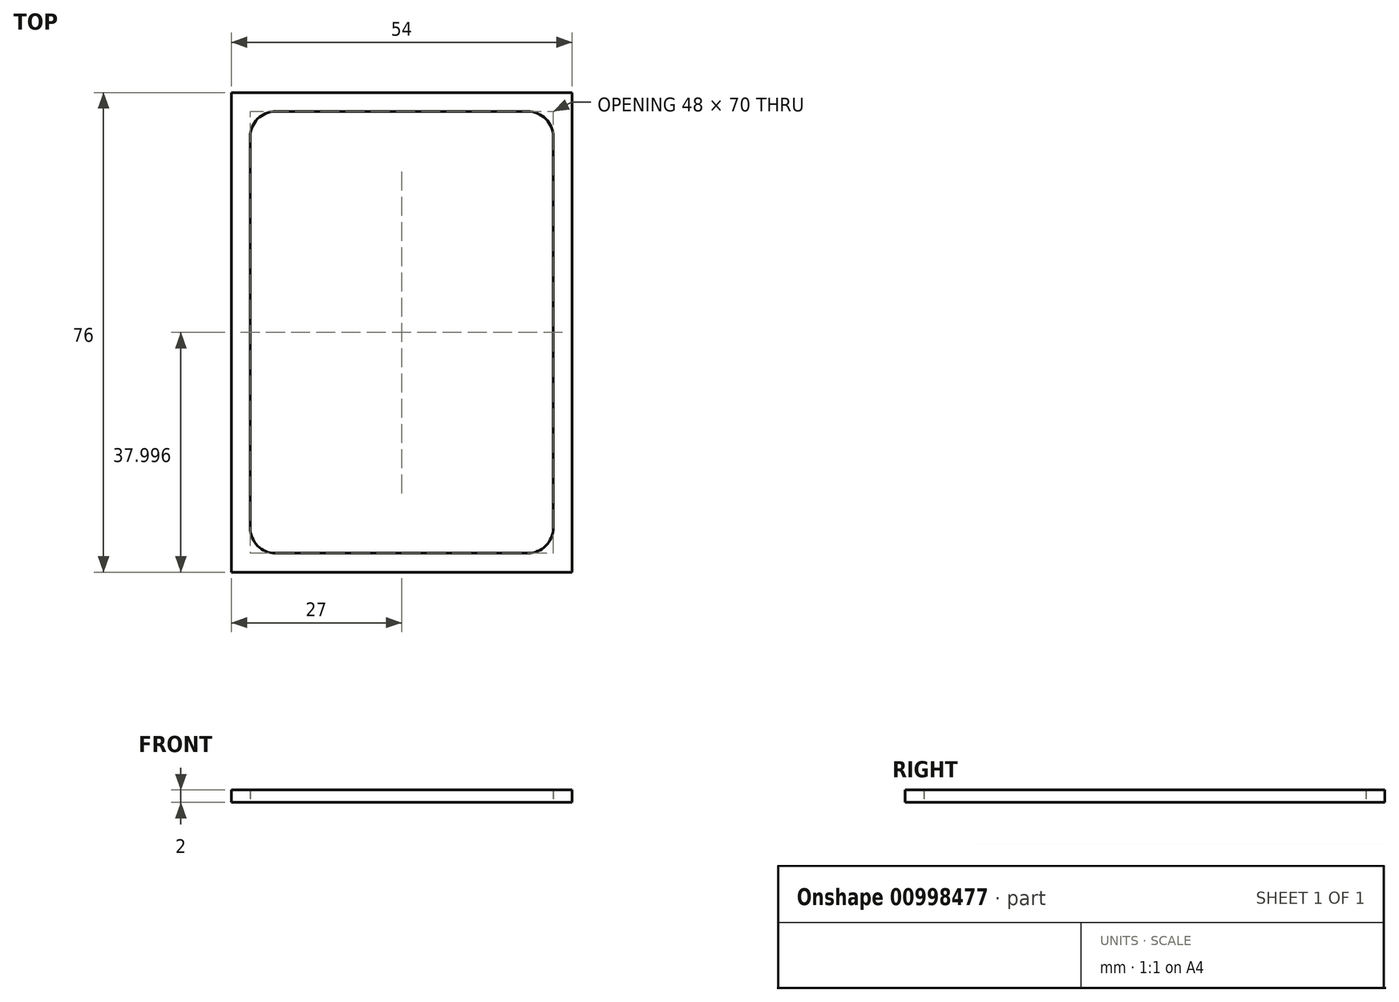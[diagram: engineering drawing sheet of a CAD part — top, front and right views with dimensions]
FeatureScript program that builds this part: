
annotation { "Feature Type Name" : "Feature", "Feature Type Description" : "" }
export const myFeature = defineFeature(function(context is Context, id is Id, definition is map)
    precondition{}
    {
        {
            var Q0;
            Q0=qCreatedBy(makeId("Top.planeOp"),FACE);
            var sketch = newSketch(context, id + "F0", { "sketchPlane" : qUnion([Q0])});
            skLineSegment(sketch, "E0.bottom", {"start": v(-27.57, 41.77) * mm, "end": v(12.43, 41.77) * mm});
            skLineSegment(sketch, "E0.top", {"start": v(-27.57, -28.23) * mm, "end": v(12.43, -28.23) * mm});
            skLineSegment(sketch, "E0.left", {"start": v(-31.57, 37.77) * mm, "end": v(-31.57, -24.23) * mm});
            skLineSegment(sketch, "E0.right", {"start": v(16.43, 37.77) * mm, "end": v(16.43, -24.23) * mm});
            skLineSegment(sketch, "E1.bottom", {"start": v(-34.57, 44.77) * mm, "end": v(19.43, 44.77) * mm});
            skLineSegment(sketch, "E1.top", {"start": v(-34.57, -31.23) * mm, "end": v(19.43, -31.23) * mm});
            skLineSegment(sketch, "E1.left", {"start": v(-34.57, 44.77) * mm, "end": v(-34.57, -31.23) * mm});
            skLineSegment(sketch, "E1.right", {"start": v(19.43, 44.77) * mm, "end": v(19.43, -31.23) * mm});
            skPoint(sketch, "E2.visualSharp", {"position": v(-31.57, 41.77) * mm});
            skArc(sketch, "E2.filletArc", {"start": v(-27.57, 41.77) * mm, "mid": v(-30.4, 40.6) * mm, "end": v(-31.57, 37.77) * mm});
            skPoint(sketch, "E3.visualSharp", {"position": v(16.43, 41.77) * mm});
            skArc(sketch, "E3.filletArc", {"start": v(16.43, 37.77) * mm, "mid": v(15.26, 40.6) * mm, "end": v(12.43, 41.77) * mm});
            skPoint(sketch, "E4.visualSharp", {"position": v(16.43, -28.23) * mm});
            skArc(sketch, "E4.filletArc", {"start": v(12.43, -28.23) * mm, "mid": v(15.26, -27.06) * mm, "end": v(16.43, -24.23) * mm});
            skPoint(sketch, "E5.visualSharp", {"position": v(-31.57, -28.23) * mm});
            skArc(sketch, "E5.filletArc", {"start": v(-31.57, -24.23) * mm, "mid": v(-30.4, -27.06) * mm, "end": v(-27.57, -28.23) * mm});
            skSolve(sketch);
        }
        {
            var Q0;
            Q0=makeQuery(id+"F0.imprint","IMPRINT",FACE,{"disambiguationData":[TD([[makeQuery(id+"F0.imprint","IMPRINT",EDGE,{"derivedFrom":sQuery(id+"F0.wireOp",EDGE,"E0.bottom")}),1.0]])]});
            extrude(context, id + "F1", {"entities" : qUnion([Q0]), "depth" : 2 * mm, "offsetDistance" : 25 * mm});
        }
    });
